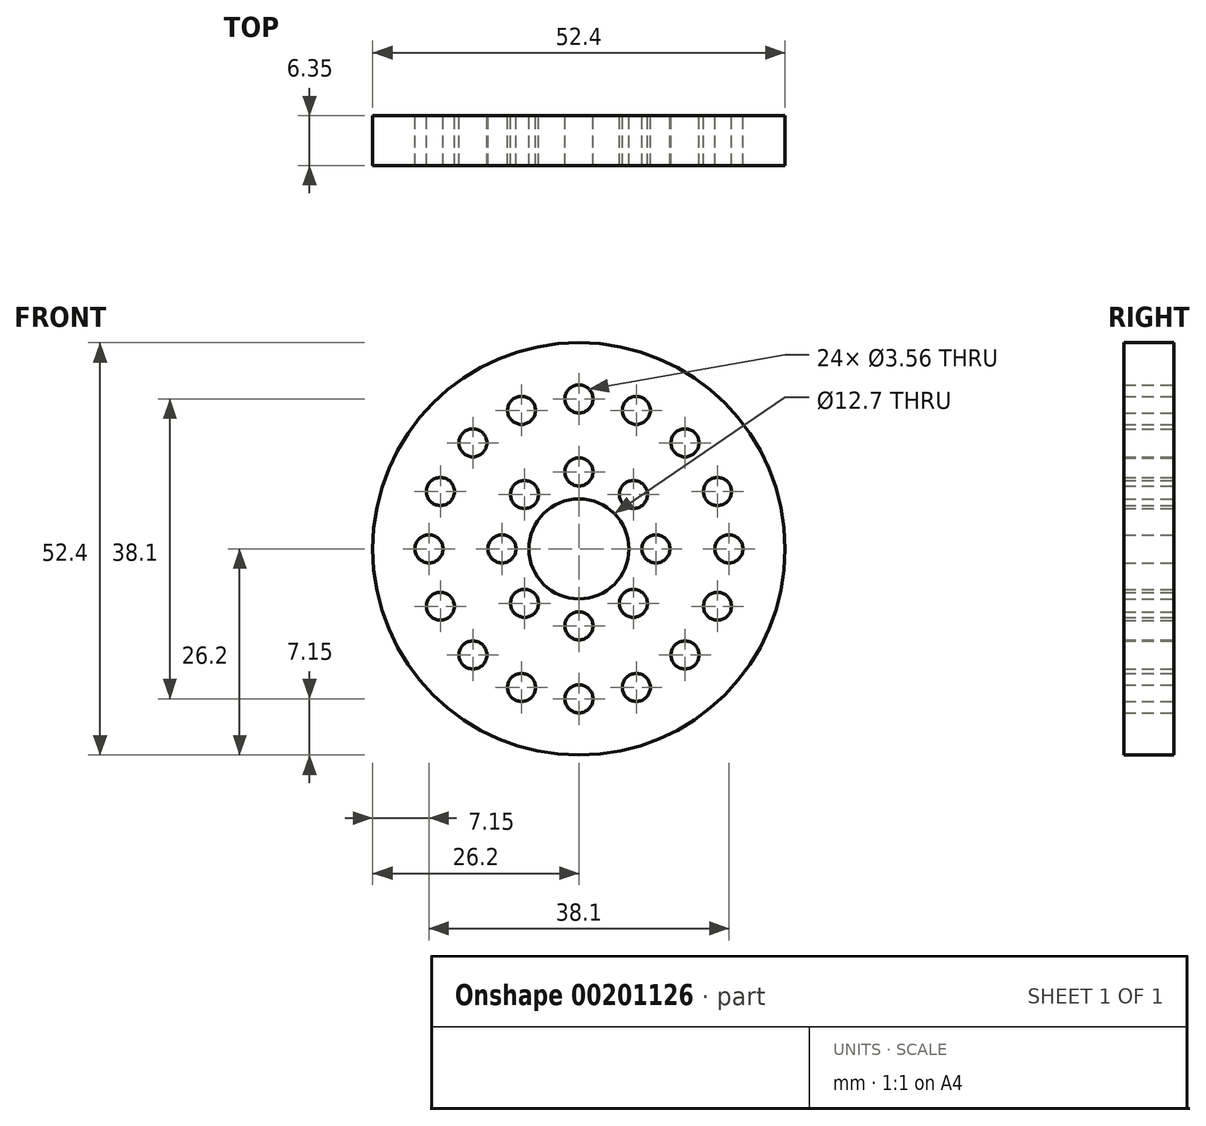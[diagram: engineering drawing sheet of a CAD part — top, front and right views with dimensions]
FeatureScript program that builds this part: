
annotation { "Feature Type Name" : "Feature", "Feature Type Description" : "" }
export const myFeature = defineFeature(function(context is Context, id is Id, definition is map)
    precondition{}
    {
        {
            var Q0;
            Q0=qCreatedBy(makeId("Front.planeOp"),FACE);
            var sketch = newSketch(context, id + "F0", { "sketchPlane" : qUnion([Q0])});
            skCircle(sketch, "E0", {"center": v(0, 0) * mm, "radius": 26.2 * mm});
            skCircle(sketch, "E1", {"center": v(0, 0) * mm, "radius": 6.35 * mm});
            skLineSegment(sketch, "E2", {"start": v(0, 0) * mm, "end": v(0, 9.78) * mm, "construction": true});
            skLineSegment(sketch, "E3", {"start": v(0, 9.78) * mm, "end": v(0, 19.05) * mm, "construction": true});
            skLineSegment(sketch, "E4", {"start": v(0, 19.05) * mm, "end": v(0, 53.48) * mm, "construction": true});
            skCircle(sketch, "E5", {"center": v(0, 9.78) * mm, "radius": 1.78 * mm});
            skCircle(sketch, "E6", {"center": v(0, 19.05) * mm, "radius": 1.78 * mm});
            skCircle(sketch, "E7.1.0", {"center": v(-6.91, 6.91) * mm, "radius": 1.78 * mm});
            skCircle(sketch, "E7.2.0", {"center": v(-9.78, 0) * mm, "radius": 1.78 * mm});
            skCircle(sketch, "E8.1.3.0", {"center": v(-6.91, -6.91) * mm, "radius": 1.78 * mm});
            skCircle(sketch, "E8.1.4.0", {"center": v(0, -9.78) * mm, "radius": 1.78 * mm});
            skCircle(sketch, "E8.1.5.0", {"center": v(6.91, -6.91) * mm, "radius": 1.78 * mm});
            skCircle(sketch, "E8.1.6.0", {"center": v(9.78, 0) * mm, "radius": 1.78 * mm});
            skCircle(sketch, "E8.1.7.0", {"center": v(6.91, 6.91) * mm, "radius": 1.78 * mm});
            skCircle(sketch, "E9.1.0", {"center": v(-7.3, 17.6) * mm, "radius": 1.78 * mm});
            skCircle(sketch, "E9.2.0", {"center": v(-13.47, 13.47) * mm, "radius": 1.78 * mm});
            skCircle(sketch, "E10.1.3.0", {"center": v(-17.6, 7.3) * mm, "radius": 1.78 * mm});
            skCircle(sketch, "E10.1.4.0", {"center": v(-19.05, 0) * mm, "radius": 1.78 * mm});
            skCircle(sketch, "E10.1.5.0", {"center": v(-17.6, -7.3) * mm, "radius": 1.78 * mm});
            skCircle(sketch, "E10.1.6.0", {"center": v(-13.47, -13.47) * mm, "radius": 1.78 * mm});
            skCircle(sketch, "E10.1.7.0", {"center": v(-7.3, -17.6) * mm, "radius": 1.78 * mm});
            skCircle(sketch, "E10.1.8.0", {"center": v(0, -19.05) * mm, "radius": 1.78 * mm});
            skCircle(sketch, "E10.1.9.0", {"center": v(7.3, -17.6) * mm, "radius": 1.78 * mm});
            skCircle(sketch, "E11.1.10.0", {"center": v(13.47, -13.47) * mm, "radius": 1.78 * mm});
            skCircle(sketch, "E11.1.11.0", {"center": v(17.6, -7.3) * mm, "radius": 1.78 * mm});
            skCircle(sketch, "E11.1.12.0", {"center": v(19.05, 0) * mm, "radius": 1.78 * mm});
            skCircle(sketch, "E11.1.13.0", {"center": v(17.6, 7.3) * mm, "radius": 1.78 * mm});
            skCircle(sketch, "E11.1.14.0", {"center": v(13.47, 13.47) * mm, "radius": 1.78 * mm});
            skCircle(sketch, "E12.1.15.0", {"center": v(7.3, 17.6) * mm, "radius": 1.78 * mm});
            skSolve(sketch);
        }
        {
            var Q0;
            Q0=makeQuery(id+"F0.imprint","IMPRINT",FACE,{"disambiguationData":[TD([[makeQuery(id+"F0.imprint","IMPRINT",EDGE,{"derivedFrom":sQuery(id+"F0.wireOp",EDGE,"E0")}),1.0]])]});
            extrude(context, id + "F1", {"entities" : qUnion([Q0]), "depth" : 6.35 * mm});
        }
    });
